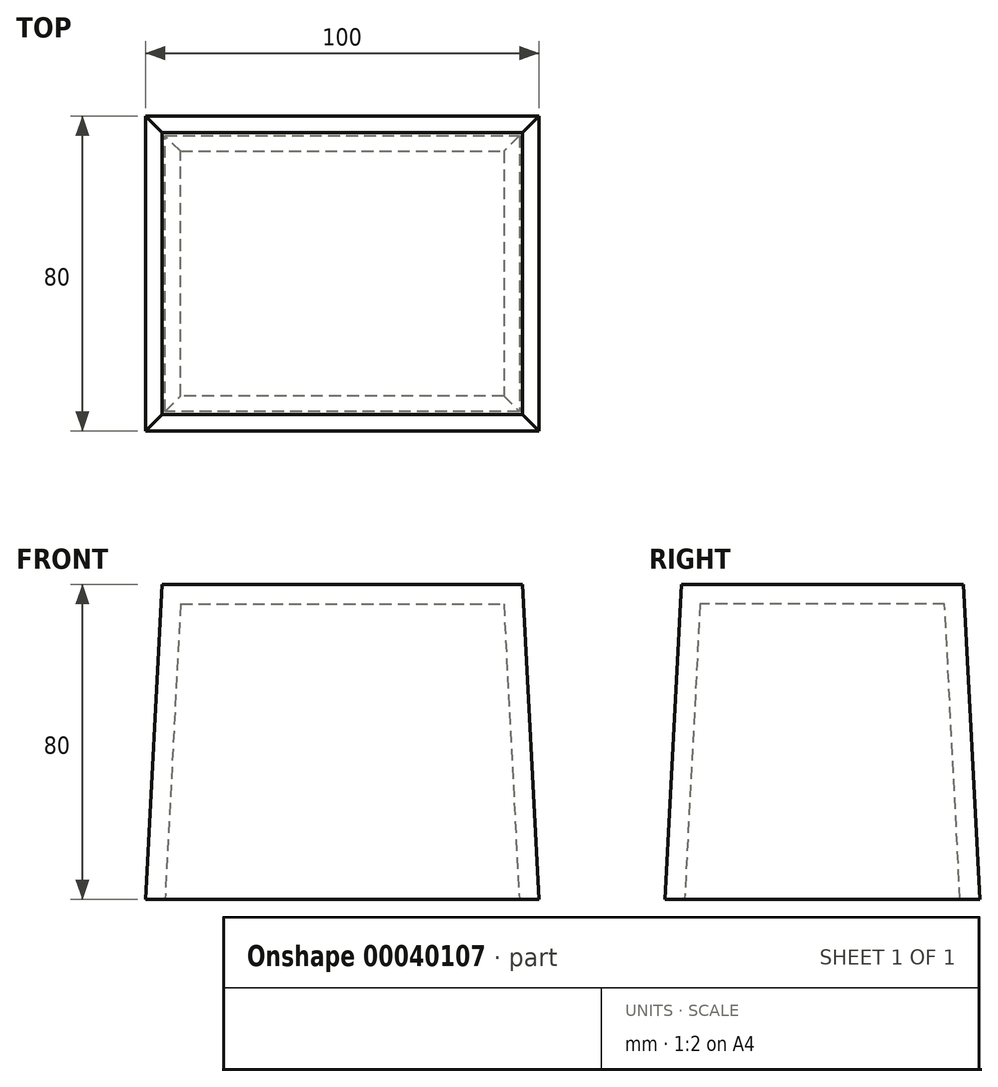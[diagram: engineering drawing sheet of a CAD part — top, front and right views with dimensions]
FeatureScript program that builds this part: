
annotation { "Feature Type Name" : "Feature", "Feature Type Description" : "" }
export const myFeature = defineFeature(function(context is Context, id is Id, definition is map)
    precondition{}
    {
        {
            var Q0;
            Q0=qCreatedBy(makeId("Top.planeOp"),FACE);
            var sketch = newSketch(context, id + "F0", { "sketchPlane" : qUnion([Q0])});
            skLineSegment(sketch, "E0.bottom", {"start": v(0, 0) * mm, "end": v(-100, 0) * mm});
            skLineSegment(sketch, "E0.top", {"start": v(0, -80) * mm, "end": v(-100, -80) * mm});
            skLineSegment(sketch, "E0.left", {"start": v(0, 0) * mm, "end": v(0, -80) * mm});
            skLineSegment(sketch, "E0.right", {"start": v(-100, 0) * mm, "end": v(-100, -80) * mm});
            skSolve(sketch);
        }
        {
            var Q0;
            Q0=makeQuery(id+"F0.imprint","IMPRINT",FACE,{"disambiguationData":[TD([[makeQuery(id+"F0.imprint","IMPRINT",EDGE,{"derivedFrom":sQuery(id+"F0.wireOp",EDGE,"E0.bottom")}),1.0]])]});
            extrude(context, id + "F1", {"entities" : qUnion([Q0]), "depth" : 80 * mm, "hasDraft" : true, "draftAngle" : 3 * degree, "draftPullDirection" : true});
        }
        {
            var Q0;
            Q0=makeQuery(id+"F1.opExtrude","CAP_FACE",FACE,{"disambiguationData":[OSD([sQuery(id+"F0.wireOp",EDGE,"E0.bottom"),sQuery(id+"F0.wireOp",EDGE,"E0.top"),sQuery(id+"F0.wireOp",EDGE,"E0.left"),sQuery(id+"F0.wireOp",EDGE,"E0.right")])],"isStart":true});
            shell(context, id + "F2", {"entities" : qUnion([Q0]), "thickness" : 5 * mm});
        }
    });
